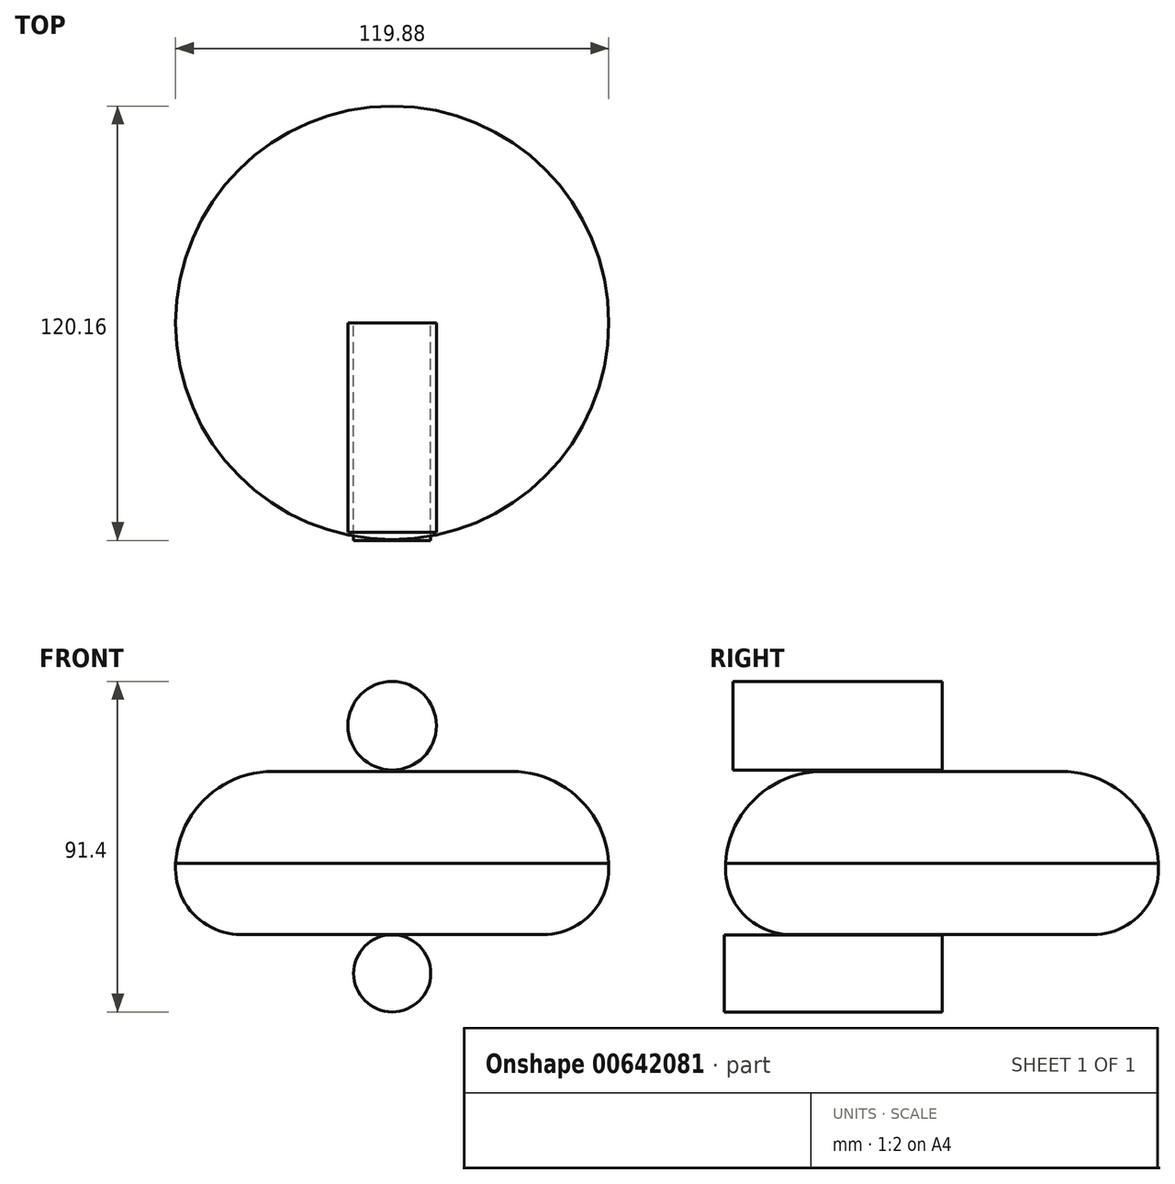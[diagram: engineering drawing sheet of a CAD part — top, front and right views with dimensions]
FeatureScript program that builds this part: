
annotation { "Feature Type Name" : "Feature", "Feature Type Description" : "" }
export const myFeature = defineFeature(function(context is Context, id is Id, definition is map)
    precondition{}
    {
        {
            var Q0;
            Q0=qCreatedBy(makeId("Top.planeOp"),FACE);
            var sketch = newSketch(context, id + "F0", { "sketchPlane" : qUnion([Q0])});
            skCircle(sketch, "E0", {"center": v(0, 0) * mm, "radius": 59.94 * mm});
            skSolve(sketch);
        }
        {
            var Q0;
            Q0=makeQuery(id+"F0.imprint","IMPRINT",FACE,{"disambiguationData":[TD([[makeQuery(id+"F0.imprint","IMPRINT",EDGE,{"derivedFrom":sQuery(id+"F0.wireOp",EDGE,"E0")}),1.0]])]});
            var sketch = newSketch(context, id + "F1", { "sketchPlane" : qUnion([Q0])});
            skSolve(sketch);
        }
        {
            var Q0;
            Q0 = qSketchRegion(id + "F1", true);
            var Q1;
            Q1=makeQuery(id+"F0.imprint","IMPRINT",FACE,{"disambiguationData":[TD([[makeQuery(id+"F0.imprint","IMPRINT",EDGE,{"derivedFrom":sQuery(id+"F0.wireOp",EDGE,"E0")}),1.0]])]});
            extrude(context, id + "F2", {"entities" : qUnion([Q0, Q1]), "depth" : 25.4 * mm, "offsetDistance" : 25.4 * mm});
        }
        {
            var Q0;
            Q0=makeQuery(id+"F2.opExtrude","CAP_FACE",FACE,{"disambiguationData":[OSD([sQuery(id+"F0.wireOp",EDGE,"E0")])],"isStart":false});
            fillet(context, id + "F3", {"entities" : qUnion([Q0]), "radius" : 26.9 * mm, "tangentPropagation" : true, "allowEdgeOverflow" : false});
        }
        {
            var Q0;
            Q0=makeQuery(id+"F1.imprint","IMPRINT",FACE,{"disambiguationData":[TD([[makeQuery(id+"F1.imprint","IMPRINT",EDGE,{"derivedFrom":makeQuery(id+"F0.imprint","IMPRINT",EDGE,{"derivedFrom":sQuery(id+"F0.wireOp",EDGE,"E0")})}),1.0]])]});
            extrude(context, id + "F4", {"entities" : qUnion([Q0]), "operationType" : NewBodyOperationType.ADD, "oppositeDirection" : true, "depth" : 19.72 * mm, "offsetDistance" : 25.4 * mm});
        }
        {
            var Q0;
            Q0=makeQuery(id+"F4.opExtrude","CAP_FACE",FACE,{"disambiguationData":[OSD([sQuery(id+"F0.wireOp",EDGE,"E0")])],"isStart":false});
            fillet(context, id + "F5", {"entities" : qUnion([Q0]), "radius" : 18.13 * mm, "tangentPropagation" : true, "allowEdgeOverflow" : false});
        }
        {
            var Q0;
            Q0=qCreatedBy(makeId("Front.planeOp"),FACE);
            var sketch = newSketch(context, id + "F6", { "sketchPlane" : qUnion([Q0])});
            skCircle(sketch, "E1", {"center": v(0, 38.05) * mm, "radius": 12.24 * mm});
            skSolve(sketch);
        }
        {
            var Q0;
            Q0 = qSketchRegion(id + "F6", true);
            extrude(context, id + "F7", {"entities" : qUnion([Q0]), "depth" : 57.9 * mm, "offsetDistance" : 25.4 * mm});
        }
        {
            var Q0;
            Q0=qCreatedBy(makeId("Front.planeOp"),FACE);
            var sketch = newSketch(context, id + "F8", { "sketchPlane" : qUnion([Q0])});
            skCircle(sketch, "E2", {"center": v(0, -30.45) * mm, "radius": 10.66 * mm});
            skSolve(sketch);
        }
        {
            var Q0;
            Q0 = qSketchRegion(id + "F8", true);
            extrude(context, id + "F9", {"entities" : qUnion([Q0]), "depth" : 60.22 * mm, "offsetDistance" : 25.4 * mm});
        }
    });
